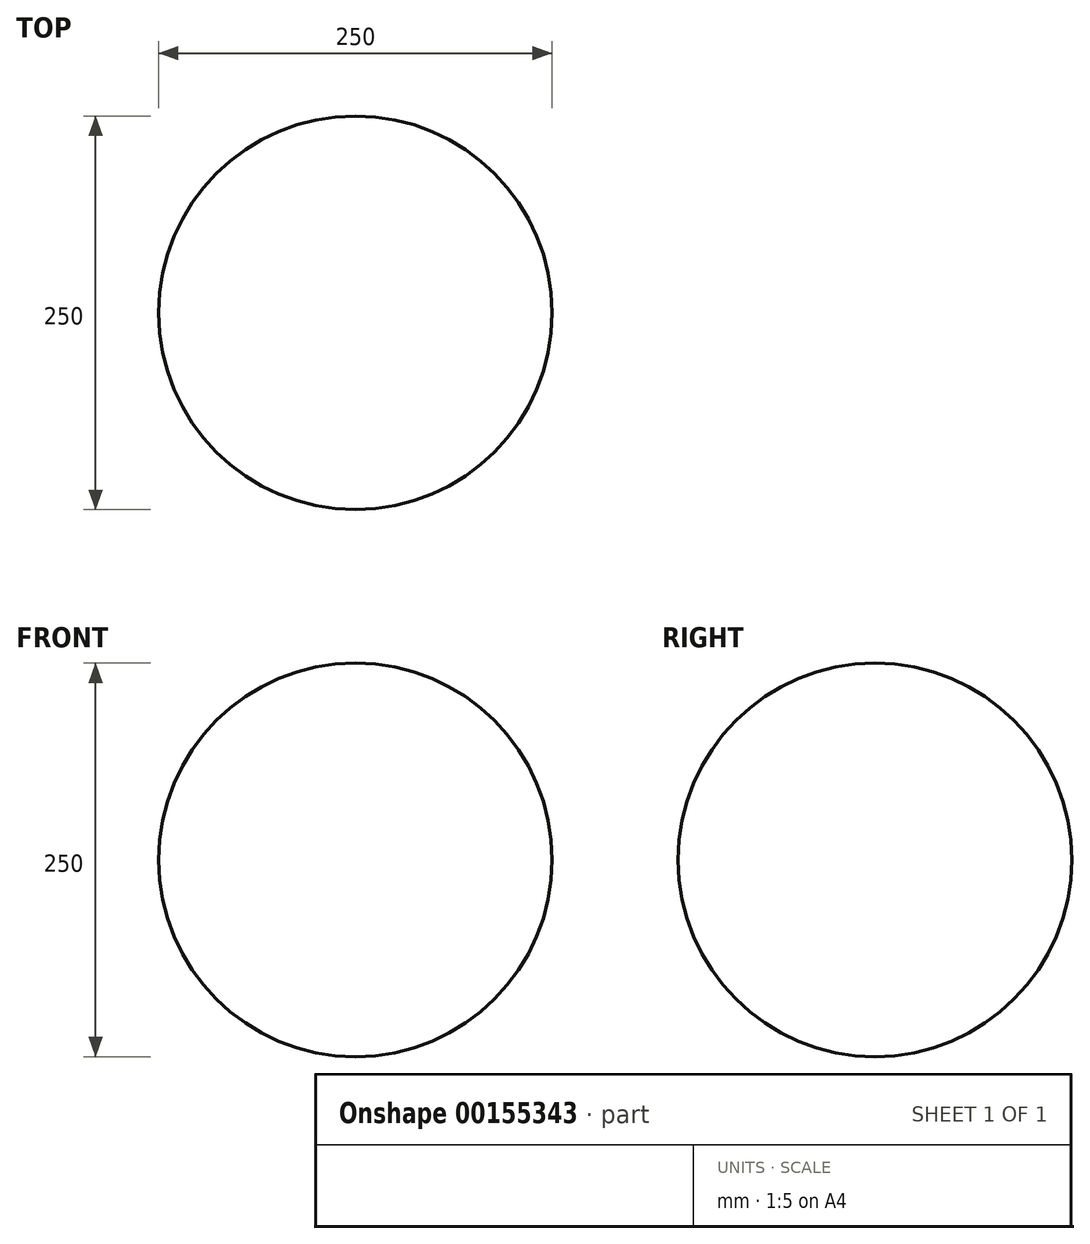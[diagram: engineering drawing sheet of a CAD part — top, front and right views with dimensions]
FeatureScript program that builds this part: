
annotation { "Feature Type Name" : "Feature", "Feature Type Description" : "" }
export const myFeature = defineFeature(function(context is Context, id is Id, definition is map)
    precondition{}
    {
        {
            var Q0;
            Q0=qCreatedBy(makeId("Front.planeOp"),FACE);
            var sketch = newSketch(context, id + "F0", { "sketchPlane" : qUnion([Q0])});
            skArc(sketch, "E0", {"start": v(25, -100) * mm, "mid": v(-100, -225) * mm, "end": v(25, -350) * mm});
            skLineSegment(sketch, "E1", {"start": v(25, -350) * mm, "end": v(25, -394.59) * mm, "construction": true});
            skLineSegment(sketch, "E2", {"start": v(25, -100) * mm, "end": v(25, -350) * mm});
            skSolve(sketch);
        }
        {
            var Q0;
            Q0=makeQuery(id+"F0.imprint","IMPRINT",FACE,{"disambiguationData":[TD([[makeQuery(id+"F0.imprint","IMPRINT",EDGE,{"derivedFrom":sQuery(id+"F0.wireOp",EDGE,"E0")}),1.0]])]});
            var Q1;
            Q1=sQuery(id+"F0.wireOp",EDGE,"E1");
            revolve(context, id + "F1", {"entities" : qUnion([Q0]), "axis" : qUnion([Q1]), "revolveType" : RevolveType.FULL});
        }
    });
